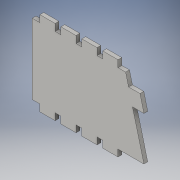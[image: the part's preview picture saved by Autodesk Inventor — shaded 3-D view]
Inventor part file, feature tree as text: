
AUTODESK INVENTOR PART (.ipt)
format: ipt  version: 2016 (Build 200138000, 138)  size: 152,064 bytes
history: native  units: in
note: dims shown in document units (in); Inventor stores cm internally (conversion verified against a paired STEP export)
features: extrude x1, sketch x1
ambient origin geometry x8: Origin, YZ Plane, XZ Plane, XY Plane, X Axis, Y Axis, Z Axis, Center Point
bodies: Body1 (feature_tree)
feature tree (2):
  extrude  "Extrusion4"  Depth=0.4in
  sketch  "Sketch1"  dims[d11=0.18in d12=0.4in d13=0.15in d14=0.4in d15=0.15in d16=0.4in d17=0.15in d18=0.4in d19=0.2in d34=0.18in d84=0.3in d85=1.15in d86=0.3978in d87=0.1in d88=0.0in]
